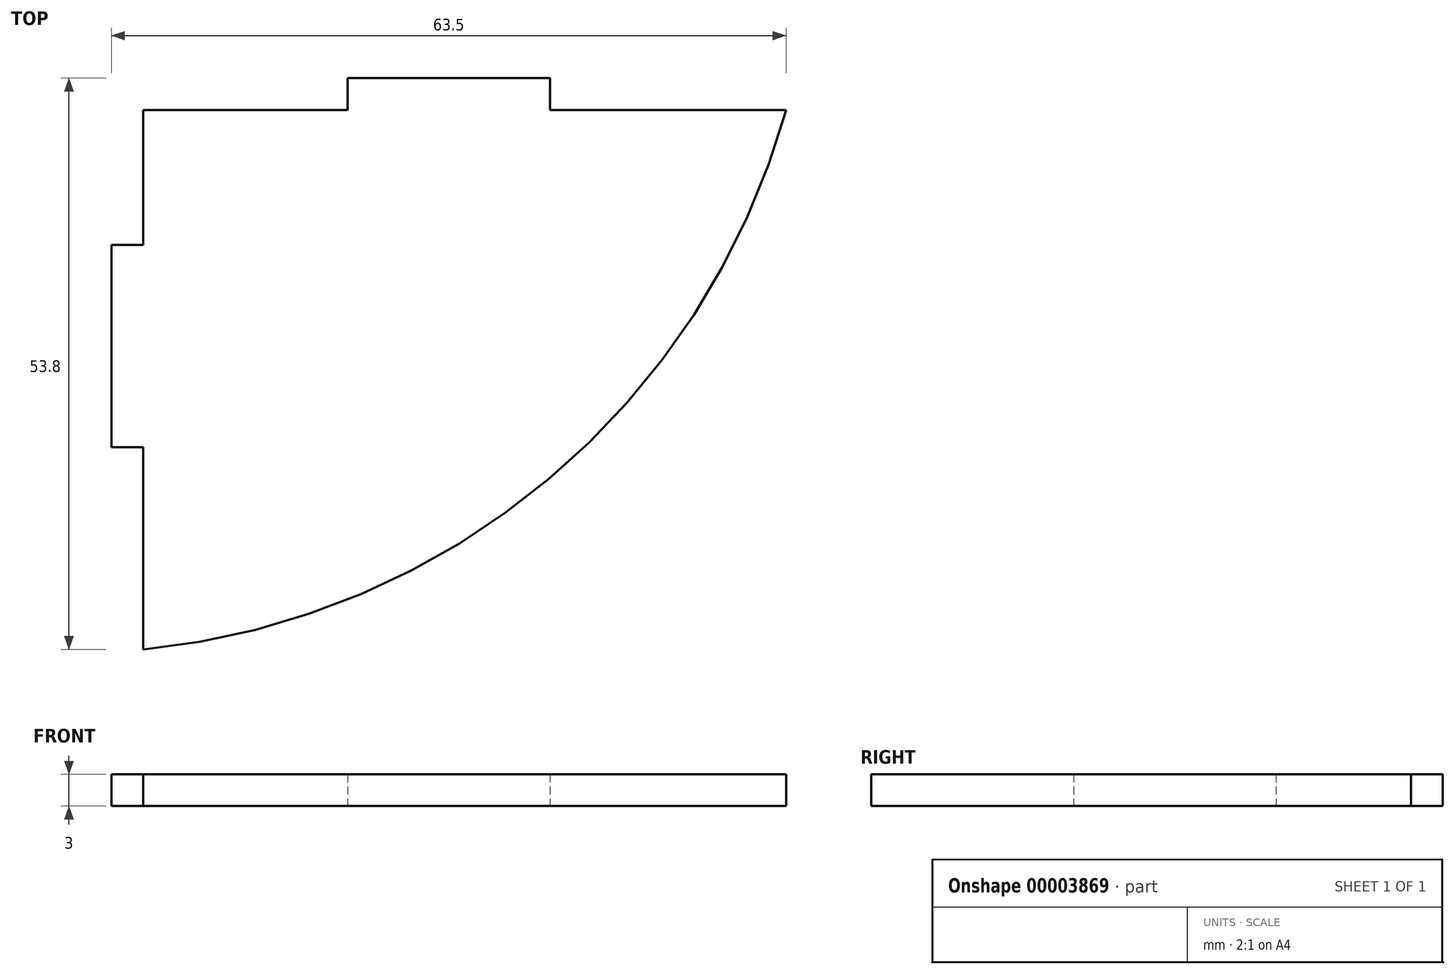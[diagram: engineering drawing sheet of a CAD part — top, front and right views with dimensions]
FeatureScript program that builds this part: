
annotation { "Feature Type Name" : "Feature", "Feature Type Description" : "" }
export const myFeature = defineFeature(function(context is Context, id is Id, definition is map)
    precondition{}
    {
        {
            var Q0;
            Q0=qCreatedBy(makeId("Top.planeOp"),FACE);
            var sketch = newSketch(context, id + "F0", { "sketchPlane" : qUnion([Q0])});
            skLineSegment(sketch, "E0", {"start": v(0, 0) * mm, "end": v(19.23, 0) * mm});
            skLineSegment(sketch, "E1", {"start": v(19.23, 0) * mm, "end": v(19.23, 3) * mm});
            skLineSegment(sketch, "E2", {"start": v(19.23, 3) * mm, "end": v(38.28, 3) * mm});
            skLineSegment(sketch, "E3", {"start": v(38.28, 3) * mm, "end": v(38.28, 0) * mm});
            skLineSegment(sketch, "E4", {"start": v(38.28, 0) * mm, "end": v(60.5, 0) * mm});
            skLineSegment(sketch, "E5", {"start": v(0, 0) * mm, "end": v(0, -12.7) * mm});
            skLineSegment(sketch, "E6", {"start": v(0, -12.7) * mm, "end": v(-3, -12.7) * mm});
            skLineSegment(sketch, "E7", {"start": v(-3, -12.7) * mm, "end": v(-3, -31.75) * mm});
            skLineSegment(sketch, "E8", {"start": v(-3, -31.75) * mm, "end": v(0, -31.75) * mm});
            skLineSegment(sketch, "E9", {"start": v(0, -31.75) * mm, "end": v(0, -50.8) * mm});
            skArc(sketch, "E10", {"start": v(0, -50.8) * mm, "mid": v(38.12, -34.78) * mm, "end": v(60.5, 0) * mm});
            skSolve(sketch);
        }
        {
            var Q0;
            Q0=makeQuery(id+"F0.imprint","IMPRINT",FACE,{"disambiguationData":[TD([[makeQuery(id+"F0.imprint","IMPRINT",EDGE,{"derivedFrom":sQuery(id+"F0.wireOp",EDGE,"E0")}),-1.0]])]});
            extrude(context, id + "F1", {"entities" : qUnion([Q0]), "depth" : 3 * mm});
        }
    });
